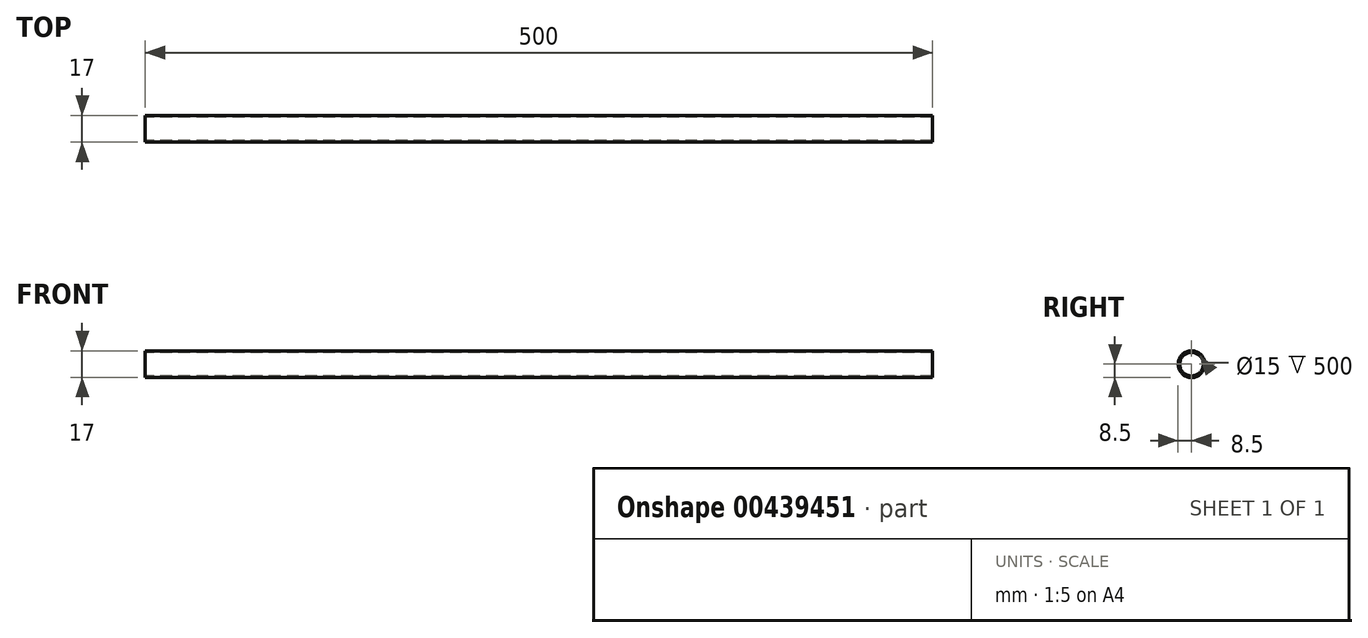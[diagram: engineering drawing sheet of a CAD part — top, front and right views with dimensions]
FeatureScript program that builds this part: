
annotation { "Feature Type Name" : "Feature", "Feature Type Description" : "" }
export const myFeature = defineFeature(function(context is Context, id is Id, definition is map)
    precondition{}
    {
        {
            var Q0;
            Q0=qCreatedBy(makeId("Right.planeOp"),FACE);
            var sketch = newSketch(context, id + "F0", { "sketchPlane" : qUnion([Q0])});
            skCircle(sketch, "E0", {"center": v(0, 0) * mm, "radius": 7.5 * mm});
            skCircle(sketch, "E1.0", {"center": v(0, 0) * mm, "radius": 8.5 * mm});
            skSolve(sketch);
        }
        {
            var Q0;
            Q0=makeQuery(id+"F0.imprint","IMPRINT",FACE,{"disambiguationData":[TD([[makeQuery(id+"F0.imprint","IMPRINT",EDGE,{"derivedFrom":sQuery(id+"F0.wireOp",EDGE,"E0")}),-1.0]])]});
            extrude(context, id + "F1", {"entities" : qUnion([Q0]), "endBound" : BoundingType.SYMMETRIC, "depth" : 500 * mm});
        }
    });
